# Revit family: 24000_Panca
name_source: partatom
category: Arredi
units: mm (PartAtom-declared; Revit-internal decimal feet)

## family parameters
Basato su piano di lavoro = Sì
Condiviso = No
Punto di calcolo locali = No
Sempre verticale = Sì
Taglio con vuoti quando caricato = No

## types (8) — shared parameters
Prospetto di default = 1219 mm
modulo = 616 mm  [stored 2.021 ft]

## per-type parameters (varying)
| type | Braccioli | Imbottiture | Struttura | dist_gamba_cen | gamba | lunghezza | num_sedute |
| 2P | No | <Per categoria> | <Per categoria> | 616 mm  [stored 2.021 ft] | No | 616 mm  [stored 2.021 ft] | 2 |
| 3P | No | <Per categoria> | <Per categoria> | 1160 mm  [stored 3.80577 ft] | No | 1232 mm  [stored 4.04199 ft] | 3 |
| 4P | No | <Per categoria> | <Per categoria> | 1160 mm  [stored 3.80577 ft] | No | 1848 mm  [stored 6.06299 ft] | 4 |
| 5P | No | <Per categoria> | <Per categoria> | 1160 mm  [stored 3.80577 ft] | Sì | 2464 mm  [stored 8.08399 ft] | 5 |
| 2P_B | Sì | <Per categoria> | <Per categoria> | 616 mm  [stored 2.021 ft] | No | 616 mm  [stored 2.021 ft] | 2 |
| 3P_B | Sì | <Per categoria> | <Per categoria> | 1160 mm  [stored 3.80577 ft] | No | 1232 mm  [stored 4.04199 ft] | 3 |
| 4P_B | Sì | 3518_Luxy_Imbottiture | 3518_Luxy_Struttura | 1160 mm  [stored 3.80577 ft] | No | 1848 mm  [stored 6.06299 ft] | 4 |
| 5P_B | Sì | <Per categoria> | <Per categoria> | 1160 mm  [stored 3.80577 ft] | Sì | 2464 mm  [stored 8.08399 ft] | 5 |

note: [stored X ft] marks values corroborated as IEEE doubles in the binary element streams (Revit-internal decimal feet)

## geometry (parser evidence)
native form markers: Sweep x12
no freeform markers — native parametric forms only
